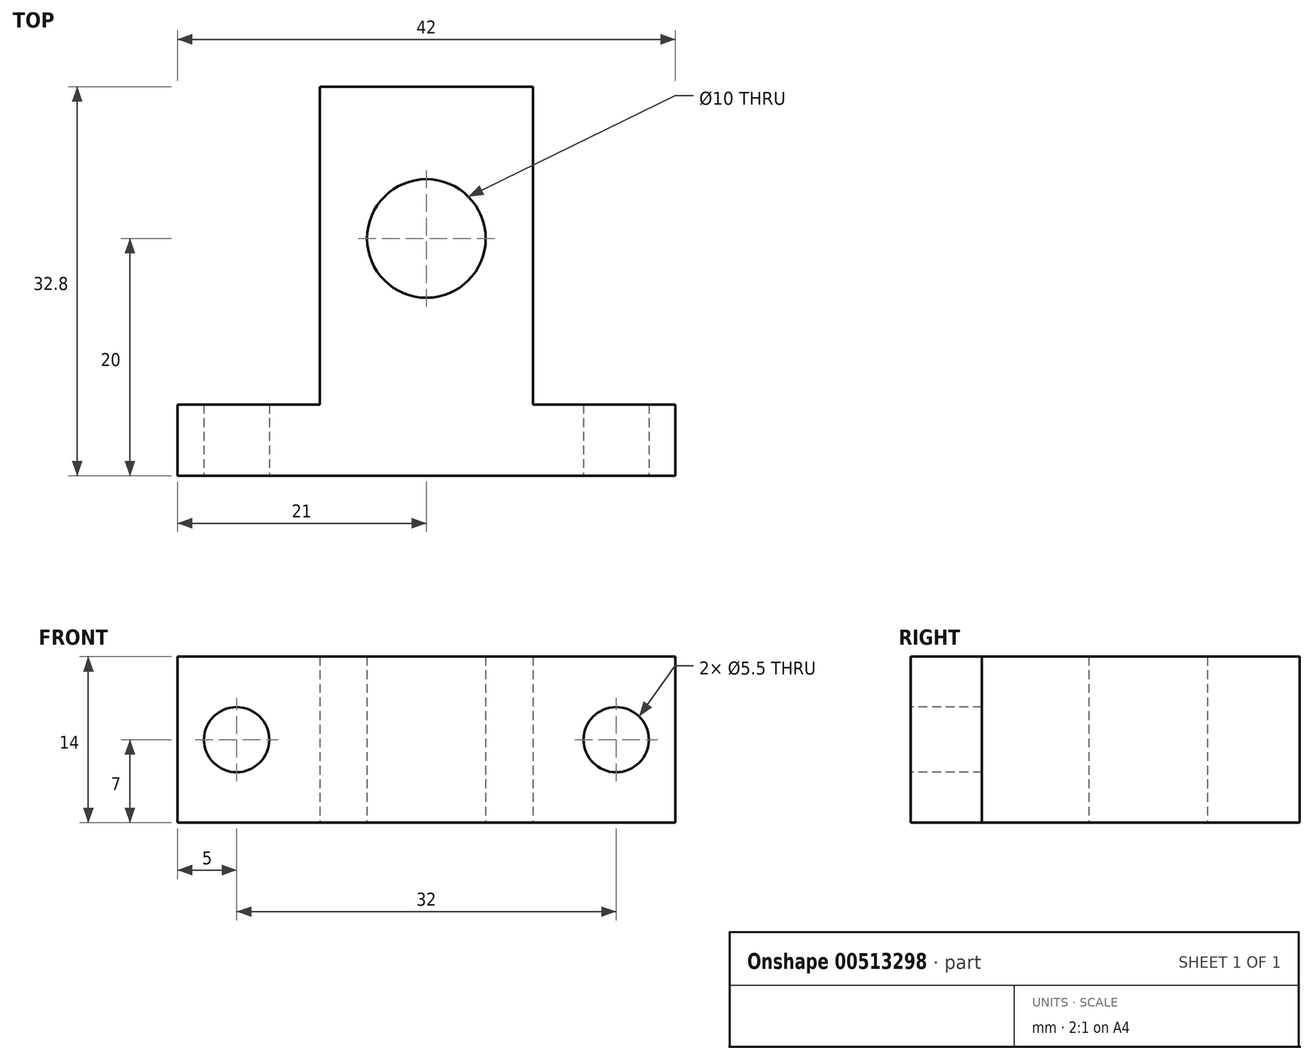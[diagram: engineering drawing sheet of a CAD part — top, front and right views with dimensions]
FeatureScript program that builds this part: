
annotation { "Feature Type Name" : "Feature", "Feature Type Description" : "" }
export const myFeature = defineFeature(function(context is Context, id is Id, definition is map)
    precondition{}
    {
        {
            var Q0;
            Q0=qCreatedBy(makeId("Top.planeOp"),FACE);
            var sketch = newSketch(context, id + "F0", { "sketchPlane" : qUnion([Q0])});
            skLineSegment(sketch, "E0", {"start": v(-9, 32.8) * mm, "end": v(9, 32.8) * mm});
            skLineSegment(sketch, "E1", {"start": v(9, 32.8) * mm, "end": v(9, 6) * mm});
            skLineSegment(sketch, "E2", {"start": v(9, 6) * mm, "end": v(21, 6) * mm});
            skLineSegment(sketch, "E3", {"start": v(21, 6) * mm, "end": v(21, 0) * mm});
            skLineSegment(sketch, "E4", {"start": v(21, 0) * mm, "end": v(-21, 0) * mm});
            skLineSegment(sketch, "E5", {"start": v(-21, 0) * mm, "end": v(-21, 6) * mm});
            skLineSegment(sketch, "E6", {"start": v(-21, 6) * mm, "end": v(-9, 6) * mm});
            skLineSegment(sketch, "E7", {"start": v(-9, 6) * mm, "end": v(-9, 32.8) * mm});
            skCircle(sketch, "E8", {"center": v(0, 20) * mm, "radius": 5 * mm});
            skSolve(sketch);
        }
        {
            var Q0;
            Q0 = qSketchRegion(id + "F0", true);
            extrude(context, id + "F1", {"entities" : qUnion([Q0]), "depth" : 14 * mm, "offsetDistance" : 25 * mm});
        }
        {
            var Q0;
            Q0=qCreatedBy(makeId("Front.planeOp"),FACE);
            var sketch = newSketch(context, id + "F2", { "sketchPlane" : qUnion([Q0])});
            skCircle(sketch, "E9", {"center": v(-16, 7) * mm, "radius": 2.75 * mm});
            skCircle(sketch, "E10.MirrorC", {"center": v(16, 7) * mm, "radius": 2.75 * mm});
            skSolve(sketch);
        }
        {
            var Q0;
            Q0 = qSketchRegion(id + "F2", true);
            extrude(context, id + "F3", {"entities" : qUnion([Q0]), "operationType" : NewBodyOperationType.REMOVE, "oppositeDirection" : true, "depth" : 6 * mm, "offsetDistance" : 25 * mm});
        }
    });
